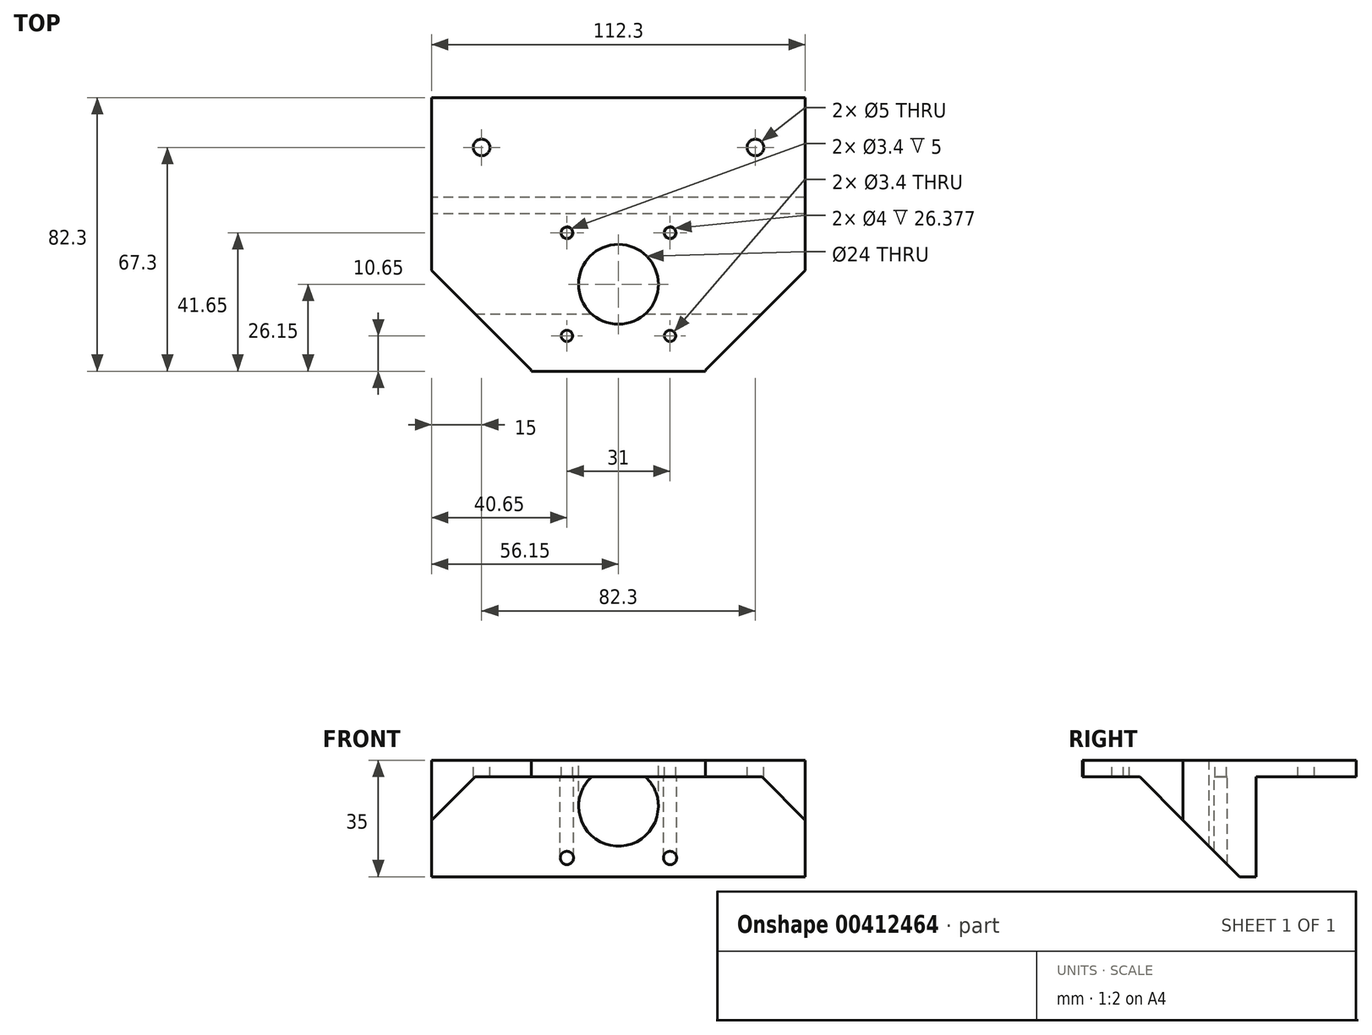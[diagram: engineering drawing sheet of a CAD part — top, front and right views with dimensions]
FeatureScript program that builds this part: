
annotation { "Feature Type Name" : "Feature", "Feature Type Description" : "" }
export const myFeature = defineFeature(function(context is Context, id is Id, definition is map)
    precondition{}
    {
        {
            var Q0;
            Q0=qCreatedBy(makeId("Top.planeOp"),FACE);
            var sketch = newSketch(context, id + "F0", { "sketchPlane" : qUnion([Q0])});
            skLineSegment(sketch, "E0.bottom", {"start": v(21.15, 21.15) * mm, "end": v(-21.15, 21.15) * mm});
            skLineSegment(sketch, "E0.top", {"start": v(21.15, -21.15) * mm, "end": v(-21.15, -21.15) * mm});
            skLineSegment(sketch, "E0.left", {"start": v(21.15, 21.15) * mm, "end": v(21.15, -21.15) * mm});
            skLineSegment(sketch, "E0.right", {"start": v(-21.15, 21.15) * mm, "end": v(-21.15, -21.15) * mm});
            skPoint(sketch, "E0.middle", {"position": v(0, 0) * mm});
            skLineSegment(sketch, "E1.bottom", {"start": v(15.5, 15.5) * mm, "end": v(-15.5, 15.5) * mm});
            skLineSegment(sketch, "E1.top", {"start": v(15.5, -15.5) * mm, "end": v(-15.5, -15.5) * mm});
            skLineSegment(sketch, "E1.left", {"start": v(15.5, 15.5) * mm, "end": v(15.5, -15.5) * mm});
            skLineSegment(sketch, "E1.right", {"start": v(-15.5, 15.5) * mm, "end": v(-15.5, -15.5) * mm});
            skCircle(sketch, "E2", {"center": v(-15.5, 15.5) * mm, "radius": 1.5 * mm});
            skCircle(sketch, "E3", {"center": v(15.5, 15.5) * mm, "radius": 1.5 * mm});
            skCircle(sketch, "E4", {"center": v(15.5, -15.5) * mm, "radius": 1.5 * mm});
            skCircle(sketch, "E5", {"center": v(-15.5, -15.5) * mm, "radius": 1.5 * mm});
            skCircle(sketch, "E6", {"center": v(0, 0) * mm, "radius": 11 * mm});
            skCircle(sketch, "E7", {"center": v(0, 0) * mm, "radius": 2.5 * mm});
            skCircle(sketch, "E8.0", {"center": v(0, 0) * mm, "radius": 12 * mm});
            skLineSegment(sketch, "E9.0", {"start": v(26.15, 26.15) * mm, "end": v(-26.15, 26.15) * mm});
            skLineSegment(sketch, "E9.1", {"start": v(26.15, 26.15) * mm, "end": v(26.15, -26.15) * mm});
            skLineSegment(sketch, "E9.2", {"start": v(26.15, -26.15) * mm, "end": v(-26.15, -26.15) * mm});
            skLineSegment(sketch, "E9.3", {"start": v(-26.15, 26.15) * mm, "end": v(-26.15, -26.15) * mm});
            skCircle(sketch, "E10.0", {"center": v(-15.5, 15.5) * mm, "radius": 1.7 * mm});
            skCircle(sketch, "E11.0", {"center": v(15.5, 15.5) * mm, "radius": 1.7 * mm});
            skCircle(sketch, "E12.0", {"center": v(15.5, -15.5) * mm, "radius": 1.7 * mm});
            skCircle(sketch, "E13.0", {"center": v(-15.5, -15.5) * mm, "radius": 1.7 * mm});
            skLineSegment(sketch, "E14.0", {"start": v(-56.15, 56.15) * mm, "end": v(-56.15, 26.15) * mm});
            skLineSegment(sketch, "E14.1", {"start": v(56.15, 56.15) * mm, "end": v(-56.15, 56.15) * mm});
            skLineSegment(sketch, "E14.2", {"start": v(56.15, 56.15) * mm, "end": v(56.15, 26.15) * mm});
            skCircle(sketch, "E15", {"center": v(-41.15, 41.15) * mm, "radius": 2.5 * mm});
            skCircle(sketch, "E16", {"center": v(41.15, 41.15) * mm, "radius": 2.5 * mm});
            skLineSegment(sketch, "E17", {"start": v(-26.15, 26.15) * mm, "end": v(-56.15, 26.15) * mm});
            skLineSegment(sketch, "E18", {"start": v(26.15, 26.15) * mm, "end": v(56.15, 26.15) * mm});
            skLineSegment(sketch, "E19", {"start": v(21.15, 21.15) * mm, "end": v(26.15, 21.15) * mm});
            skLineSegment(sketch, "E20", {"start": v(-21.15, 21.15) * mm, "end": v(-26.15, 21.15) * mm});
            skLineSegment(sketch, "E21.bottom", {"start": v(-26.15, 21.15) * mm, "end": v(-56.15, 21.15) * mm});
            skLineSegment(sketch, "E21.left", {"start": v(-26.15, 21.15) * mm, "end": v(-26.15, 26.15) * mm});
            skLineSegment(sketch, "E21.right", {"start": v(-56.15, 21.15) * mm, "end": v(-56.15, 26.15) * mm});
            skLineSegment(sketch, "E22.bottom", {"start": v(26.15, 21.15) * mm, "end": v(56.15, 21.15) * mm});
            skLineSegment(sketch, "E22.left", {"start": v(26.15, 21.15) * mm, "end": v(26.15, 26.15) * mm});
            skLineSegment(sketch, "E22.right", {"start": v(56.15, 21.15) * mm, "end": v(56.15, 26.15) * mm});
            skCircle(sketch, "E23", {"center": v(15.5, 15.5) * mm, "radius": 2 * mm});
            skCircle(sketch, "E24", {"center": v(-15.5, -15.5) * mm, "radius": 2 * mm});
            skCircle(sketch, "E25", {"center": v(-15.5, 15.5) * mm, "radius": 2 * mm});
            skCircle(sketch, "E26", {"center": v(15.5, -15.5) * mm, "radius": 2 * mm});
            skSolve(sketch);
        }
        {
            var Q0;
            Q0=makeQuery(id+"F0.imprint","IMPRINT",FACE,{"disambiguationData":[TD([[makeQuery(id+"F0.imprint","IMPRINT",EDGE,{"derivedFrom":sQuery(id+"F0.wireOp",EDGE,"E0.bottom")}),-1.0]])]});
            var Q1;
            Q1=makeQuery(id+"F0.imprint","IMPRINT",FACE,{"disambiguationData":[TD([[makeQuery(id+"F0.imprint","IMPRINT",EDGE,{"derivedFrom":sQuery(id+"F0.wireOp",EDGE,"E0.bottom")}),1.0]])]});
            var Q2;
            Q2=makeQuery(id+"F0.imprint","IMPRINT",FACE,{"disambiguationData":[TD([[makeQuery(id+"F0.imprint","IMPRINT",EDGE,{"derivedFrom":sQuery(id+"F0.wireOp",EDGE,"E8.0")}),-1.0]])]});
            var Q3;
            Q3=makeQuery(id+"F0.imprint","IMPRINT",FACE,{"disambiguationData":[TD([[makeQuery(id+"F0.imprint","IMPRINT",EDGE,{"derivedFrom":sQuery(id+"F0.wireOp",EDGE,"E9.0")}),-1.0]])]});
            var Q4;
            Q4=makeQuery(id+"F0.imprint","IMPRINT",FACE,{"disambiguationData":[TD([[makeQuery(id+"F0.imprint","IMPRINT",EDGE,{"derivedFrom":sQuery(id+"F0.wireOp",EDGE,"E0.top")}),1.0]])]});
            var Q5;
            Q5=makeQuery(id+"F0.imprint","IMPRINT",FACE,{"disambiguationData":[TD([[makeQuery(id+"F0.imprint","IMPRINT",EDGE,{"derivedFrom":sQuery(id+"F0.wireOp",EDGE,"E21.bottom")}),-1.0]])]});
            var Q6;
            Q6=makeQuery(id+"F0.imprint","IMPRINT",FACE,{"disambiguationData":[TD([[makeQuery(id+"F0.imprint","IMPRINT",EDGE,{"derivedFrom":sQuery(id+"F0.wireOp",EDGE,"E22.bottom")}),1.0]])]});
            var Q7;
            {var subQ0=sQuery(id+"F0.wireOp",EDGE,"E11.0");var subQ1=sQuery(id+"F0.wireOp",EDGE,"E1.bottom");var subQ2=makeQuery(id+"F0.imprint","INTERSECT",VERTEX,{"derivedFrom":[subQ1,subQ0]});Q7=makeQuery(id+"F0.imprint","IMPRINT",FACE,{"disambiguationData":[TD([[makeQuery(id+"F0.imprint","IMPRINT",EDGE,{"disambiguationData":[TD([[subQ2,-1.0]])],"derivedFrom":subQ1}),-1.0]])]});}
            var Q8;
            {var subQ0=sQuery(id+"F0.wireOp",EDGE,"E11.0");var subQ1=sQuery(id+"F0.wireOp",EDGE,"E1.bottom");var subQ2=makeQuery(id+"F0.imprint","INTERSECT",VERTEX,{"derivedFrom":[subQ1,subQ0]});Q8=makeQuery(id+"F0.imprint","IMPRINT",FACE,{"disambiguationData":[TD([[makeQuery(id+"F0.imprint","IMPRINT",EDGE,{"disambiguationData":[TD([[subQ2,-1.0]])],"derivedFrom":subQ1}),1.0]])]});}
            var Q9;
            {var subQ0=sQuery(id+"F0.wireOp",EDGE,"E12.0");var subQ1=sQuery(id+"F0.wireOp",EDGE,"E1.top");var subQ2=makeQuery(id+"F0.imprint","INTERSECT",VERTEX,{"derivedFrom":[subQ1,subQ0]});Q9=makeQuery(id+"F0.imprint","IMPRINT",FACE,{"disambiguationData":[TD([[makeQuery(id+"F0.imprint","IMPRINT",EDGE,{"disambiguationData":[TD([[subQ2,-1.0]])],"derivedFrom":subQ1}),1.0]])]});}
            var Q10;
            {var subQ0=sQuery(id+"F0.wireOp",EDGE,"E12.0");var subQ1=sQuery(id+"F0.wireOp",EDGE,"E1.top");var subQ2=makeQuery(id+"F0.imprint","INTERSECT",VERTEX,{"derivedFrom":[subQ1,subQ0]});Q10=makeQuery(id+"F0.imprint","IMPRINT",FACE,{"disambiguationData":[TD([[makeQuery(id+"F0.imprint","IMPRINT",EDGE,{"disambiguationData":[TD([[subQ2,-1.0]])],"derivedFrom":subQ1}),-1.0]])]});}
            var Q11;
            {var subQ0=sQuery(id+"F0.wireOp",EDGE,"E24");var subQ1=sQuery(id+"F0.wireOp",EDGE,"E1.top");var subQ2=makeQuery(id+"F0.imprint","INTERSECT",VERTEX,{"derivedFrom":[subQ1,subQ0]});Q11=makeQuery(id+"F0.imprint","IMPRINT",FACE,{"disambiguationData":[TD([[makeQuery(id+"F0.imprint","IMPRINT",EDGE,{"disambiguationData":[TD([[subQ2,-1.0]])],"derivedFrom":subQ1}),1.0]])]});}
            var Q12;
            {var subQ0=sQuery(id+"F0.wireOp",EDGE,"E24");var subQ1=sQuery(id+"F0.wireOp",EDGE,"E1.top");var subQ2=makeQuery(id+"F0.imprint","INTERSECT",VERTEX,{"derivedFrom":[subQ1,subQ0]});Q12=makeQuery(id+"F0.imprint","IMPRINT",FACE,{"disambiguationData":[TD([[makeQuery(id+"F0.imprint","IMPRINT",EDGE,{"disambiguationData":[TD([[subQ2,-1.0]])],"derivedFrom":subQ1}),-1.0]])]});}
            var Q13;
            {var subQ0=sQuery(id+"F0.wireOp",EDGE,"E25");var subQ1=sQuery(id+"F0.wireOp",EDGE,"E1.bottom");var subQ2=makeQuery(id+"F0.imprint","INTERSECT",VERTEX,{"derivedFrom":[subQ1,subQ0]});Q13=makeQuery(id+"F0.imprint","IMPRINT",FACE,{"disambiguationData":[TD([[makeQuery(id+"F0.imprint","IMPRINT",EDGE,{"disambiguationData":[TD([[subQ2,-1.0]])],"derivedFrom":subQ1}),-1.0]])]});}
            var Q14;
            {var subQ0=sQuery(id+"F0.wireOp",EDGE,"E25");var subQ1=sQuery(id+"F0.wireOp",EDGE,"E1.bottom");var subQ2=makeQuery(id+"F0.imprint","INTERSECT",VERTEX,{"derivedFrom":[subQ1,subQ0]});Q14=makeQuery(id+"F0.imprint","IMPRINT",FACE,{"disambiguationData":[TD([[makeQuery(id+"F0.imprint","IMPRINT",EDGE,{"disambiguationData":[TD([[subQ2,-1.0]])],"derivedFrom":subQ1}),1.0]])]});}
            extrude(context, id + "F1", {"entities" : qUnion([Q0, Q1, Q2, Q3, Q4, Q5, Q6, Q7, Q8, Q9, Q10, Q11, Q12, Q13, Q14]), "oppositeDirection" : true, "depth" : 5 * mm});
        }
        {
            var Q0;
            Q0=makeQuery(id+"F1.opExtrude","SWEPT_EDGE",EDGE,{"disambiguationData":[OSD([sQuery(id+"F0.wireOp",EDGE,"E9.3"),sQuery(id+"F0.wireOp",EDGE,"E20"),sQuery(id+"F0.wireOp",EDGE,"E21.bottom"),sQuery(id+"F0.wireOp",EDGE,"E21.left")])]});
            var Q1;
            Q1=makeQuery(id+"F1.opExtrude","SWEPT_EDGE",EDGE,{"disambiguationData":[OSD([sQuery(id+"F0.wireOp",EDGE,"E9.1"),sQuery(id+"F0.wireOp",EDGE,"E19"),sQuery(id+"F0.wireOp",EDGE,"E22.bottom"),sQuery(id+"F0.wireOp",EDGE,"E22.left")])]});
            chamfer(context, id + "F2", {"entities" : qUnion([Q0, Q1]), "width" : 47 * mm, "tangentPropagation" : true});
        }
        {
            var Q0;
            Q0=makeQuery(id+"F0.imprint","IMPRINT",FACE,{"disambiguationData":[TD([[makeQuery(id+"F0.imprint","IMPRINT",EDGE,{"derivedFrom":sQuery(id+"F0.wireOp",EDGE,"E0.bottom")}),-1.0]])]});
            var Q1;
            Q1=makeQuery(id+"F0.imprint","IMPRINT",FACE,{"disambiguationData":[TD([[makeQuery(id+"F0.imprint","IMPRINT",EDGE,{"derivedFrom":sQuery(id+"F0.wireOp",EDGE,"E21.bottom")}),-1.0]])]});
            var Q2;
            Q2=makeQuery(id+"F0.imprint","IMPRINT",FACE,{"disambiguationData":[TD([[makeQuery(id+"F0.imprint","IMPRINT",EDGE,{"derivedFrom":sQuery(id+"F0.wireOp",EDGE,"E22.bottom")}),1.0]])]});
            extrude(context, id + "F3", {"entities" : qUnion([Q0, Q1, Q2]), "operationType" : NewBodyOperationType.ADD, "oppositeDirection" : true, "depth" : 35 * mm});
        }
        {
            var Q0;
            {var subQ0=sQuery(id+"F0.wireOp",EDGE,"E22.bottom");var subQ1=sQuery(id+"F0.wireOp",EDGE,"E21.bottom");Q0=makeQuery(id+"F3.boolean.opBoolean","INTERSECT",EDGE,{"derivedFrom":[makeQuery(id+"F1.opExtrude","CAP_FACE",FACE,{"disambiguationData":[OSD([sQuery(id+"F0.wireOp",EDGE,"E8.0"),sQuery(id+"F0.wireOp",EDGE,"E9.1"),sQuery(id+"F0.wireOp",EDGE,"E9.2"),sQuery(id+"F0.wireOp",EDGE,"E9.3"),sQuery(id+"F0.wireOp",EDGE,"E10.0"),sQuery(id+"F0.wireOp",EDGE,"E11.0"),sQuery(id+"F0.wireOp",EDGE,"E12.0"),sQuery(id+"F0.wireOp",EDGE,"E13.0"),sQuery(id+"F0.wireOp",EDGE,"E14.0"),sQuery(id+"F0.wireOp",EDGE,"E14.1"),sQuery(id+"F0.wireOp",EDGE,"E14.2"),sQuery(id+"F0.wireOp",EDGE,"E15"),sQuery(id+"F0.wireOp",EDGE,"E16"),subQ1,sQuery(id+"F0.wireOp",EDGE,"E21.right"),subQ0,sQuery(id+"F0.wireOp",EDGE,"E22.right")])],"isStart":false}),makeQuery(id+"F3.opExtrude","SWEPT_FACE",FACE,{"disambiguationData":[OSD([sQuery(id+"F0.wireOp",EDGE,"E0.bottom"),sQuery(id+"F0.wireOp",EDGE,"E19"),sQuery(id+"F0.wireOp",EDGE,"E20"),subQ1,subQ0])]})]});}
            chamfer(context, id + "F4", {"entities" : qUnion([Q0]), "width" : 30 * mm, "tangentPropagation" : true});
        }
        {
            var Q0;
            {var subQ0=sQuery(id+"F0.wireOp",EDGE,"E11.0");var subQ1=sQuery(id+"F0.wireOp",EDGE,"E1.bottom");var subQ2=makeQuery(id+"F0.imprint","INTERSECT",VERTEX,{"derivedFrom":[subQ1,subQ0]});Q0=makeQuery(id+"F0.imprint","IMPRINT",FACE,{"disambiguationData":[TD([[makeQuery(id+"F0.imprint","IMPRINT",EDGE,{"disambiguationData":[TD([[subQ2,-1.0]])],"derivedFrom":subQ1}),-1.0]])]});}
            var Q1;
            {var subQ0=sQuery(id+"F0.wireOp",EDGE,"E11.0");var subQ1=sQuery(id+"F0.wireOp",EDGE,"E1.bottom");var subQ2=makeQuery(id+"F0.imprint","INTERSECT",VERTEX,{"derivedFrom":[subQ1,subQ0]});Q1=makeQuery(id+"F0.imprint","IMPRINT",FACE,{"disambiguationData":[TD([[makeQuery(id+"F0.imprint","IMPRINT",EDGE,{"disambiguationData":[TD([[subQ2,-1.0]])],"derivedFrom":subQ1}),1.0]])]});}
            var Q2;
            {var subQ0=sQuery(id+"F0.wireOp",EDGE,"E1.left");var subQ1=sQuery(id+"F0.wireOp",EDGE,"E1.bottom");var subQ2=makeQuery(id+"F0.imprint","INTERSECT",VERTEX,{"derivedFrom":[subQ1,subQ0]});Q2=makeQuery(id+"F0.imprint","IMPRINT",FACE,{"disambiguationData":[TD([[makeQuery(id+"F0.imprint","IMPRINT",EDGE,{"disambiguationData":[TD([[subQ2,-1.0]])],"derivedFrom":subQ1}),-1.0]])]});}
            extrude(context, id + "F5", {"entities" : qUnion([Q0, Q1, Q2]), "operationType" : NewBodyOperationType.REMOVE, "oppositeDirection" : true, "depth" : 30 * mm, "hasSecondDirection" : true, "secondDirectionOppositeDirection" : true, "secondDirectionDepth" : 5 * mm});
        }
        {
            var Q0;
            {var subQ0=sQuery(id+"F0.wireOp",EDGE,"E11.0");var subQ1=sQuery(id+"F0.wireOp",EDGE,"E1.bottom");var subQ2=makeQuery(id+"F0.imprint","INTERSECT",VERTEX,{"derivedFrom":[subQ1,subQ0]});Q0=makeQuery(id+"F0.imprint","IMPRINT",FACE,{"disambiguationData":[TD([[makeQuery(id+"F0.imprint","IMPRINT",EDGE,{"disambiguationData":[TD([[subQ2,-1.0]])],"derivedFrom":subQ1}),-1.0]])]});}
            var Q1;
            {var subQ0=sQuery(id+"F0.wireOp",EDGE,"E11.0");var subQ1=sQuery(id+"F0.wireOp",EDGE,"E1.bottom");var subQ2=makeQuery(id+"F0.imprint","INTERSECT",VERTEX,{"derivedFrom":[subQ1,subQ0]});Q1=makeQuery(id+"F0.imprint","IMPRINT",FACE,{"disambiguationData":[TD([[makeQuery(id+"F0.imprint","IMPRINT",EDGE,{"disambiguationData":[TD([[subQ2,-1.0]])],"derivedFrom":subQ1}),1.0]])]});}
            var Q2;
            {var subQ0=sQuery(id+"F0.wireOp",EDGE,"E12.0");var subQ1=sQuery(id+"F0.wireOp",EDGE,"E1.top");var subQ2=makeQuery(id+"F0.imprint","INTERSECT",VERTEX,{"derivedFrom":[subQ1,subQ0]});Q2=makeQuery(id+"F0.imprint","IMPRINT",FACE,{"disambiguationData":[TD([[makeQuery(id+"F0.imprint","IMPRINT",EDGE,{"disambiguationData":[TD([[subQ2,-1.0]])],"derivedFrom":subQ1}),1.0]])]});}
            var Q3;
            {var subQ0=sQuery(id+"F0.wireOp",EDGE,"E12.0");var subQ1=sQuery(id+"F0.wireOp",EDGE,"E1.top");var subQ2=makeQuery(id+"F0.imprint","INTERSECT",VERTEX,{"derivedFrom":[subQ1,subQ0]});Q3=makeQuery(id+"F0.imprint","IMPRINT",FACE,{"disambiguationData":[TD([[makeQuery(id+"F0.imprint","IMPRINT",EDGE,{"disambiguationData":[TD([[subQ2,-1.0]])],"derivedFrom":subQ1}),-1.0]])]});}
            var Q4;
            {var subQ0=sQuery(id+"F0.wireOp",EDGE,"E24");var subQ1=sQuery(id+"F0.wireOp",EDGE,"E1.top");var subQ2=makeQuery(id+"F0.imprint","INTERSECT",VERTEX,{"derivedFrom":[subQ1,subQ0]});Q4=makeQuery(id+"F0.imprint","IMPRINT",FACE,{"disambiguationData":[TD([[makeQuery(id+"F0.imprint","IMPRINT",EDGE,{"disambiguationData":[TD([[subQ2,-1.0]])],"derivedFrom":subQ1}),1.0]])]});}
            var Q5;
            {var subQ0=sQuery(id+"F0.wireOp",EDGE,"E24");var subQ1=sQuery(id+"F0.wireOp",EDGE,"E1.top");var subQ2=makeQuery(id+"F0.imprint","INTERSECT",VERTEX,{"derivedFrom":[subQ1,subQ0]});Q5=makeQuery(id+"F0.imprint","IMPRINT",FACE,{"disambiguationData":[TD([[makeQuery(id+"F0.imprint","IMPRINT",EDGE,{"disambiguationData":[TD([[subQ2,-1.0]])],"derivedFrom":subQ1}),-1.0]])]});}
            var Q6;
            {var subQ0=sQuery(id+"F0.wireOp",EDGE,"E25");var subQ1=sQuery(id+"F0.wireOp",EDGE,"E1.bottom");var subQ2=makeQuery(id+"F0.imprint","INTERSECT",VERTEX,{"derivedFrom":[subQ1,subQ0]});Q6=makeQuery(id+"F0.imprint","IMPRINT",FACE,{"disambiguationData":[TD([[makeQuery(id+"F0.imprint","IMPRINT",EDGE,{"disambiguationData":[TD([[subQ2,-1.0]])],"derivedFrom":subQ1}),-1.0]])]});}
            var Q7;
            {var subQ0=sQuery(id+"F0.wireOp",EDGE,"E25");var subQ1=sQuery(id+"F0.wireOp",EDGE,"E1.bottom");var subQ2=makeQuery(id+"F0.imprint","INTERSECT",VERTEX,{"derivedFrom":[subQ1,subQ0]});Q7=makeQuery(id+"F0.imprint","IMPRINT",FACE,{"disambiguationData":[TD([[makeQuery(id+"F0.imprint","IMPRINT",EDGE,{"disambiguationData":[TD([[subQ2,-1.0]])],"derivedFrom":subQ1}),1.0]])]});}
            extrude(context, id + "F6", {"entities" : qUnion([Q0, Q1, Q2, Q3, Q4, Q5, Q6, Q7]), "operationType" : NewBodyOperationType.REMOVE, "oppositeDirection" : true, "depth" : 35 * mm, "hasSecondDirection" : true, "secondDirectionOppositeDirection" : true, "secondDirectionDepth" : 5 * mm});
        }
    });
